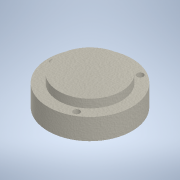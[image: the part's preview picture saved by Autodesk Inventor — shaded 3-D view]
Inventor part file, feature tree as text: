
AUTODESK INVENTOR PART (.ipt)
format: ipt  version: 2022.1 (Build 261234000, 234)  size: 149,504 bytes
history: native  units: mm
features: extrude x3, sketch x3, other x1
ambient origin geometry x8: Origin, YZ Plane, XZ Plane, XY Plane, X Axis, Y Axis, Z Axis, Center Point
bodies: Body1 (feature_tree)
feature tree (7):
  other  "Sólido1"
  extrude  "Extrusión1"  Depth=40.0mm
  extrude  "Extrusión2"  Depth=3.0mm
  extrude  "Extrusión3"  TaperAngle=120.0deg  [1 undecoded]
  sketch  "Boceto1"  dims[d4=25.0mm d5=40.0mm]
  sketch  "Boceto2"  dims[d6=3.0mm d7=3.0mm]
  sketch  "Boceto3"  dims[d8=3.0mm d10=120.0deg d11=120.0deg d12=17.5mm d13=17.5mm d14=17.5mm d15=10.0mm d16=0.0mm d17=30.0mm d18=2.5mm d19=0.0mm d20=1.5mm d21=0.0mm]
note: 1 required parameter value undecoded (feature->parameter linkage not recoverable at this tier; creation-order binding heuristic only, values carry confidence <= 0.55)
